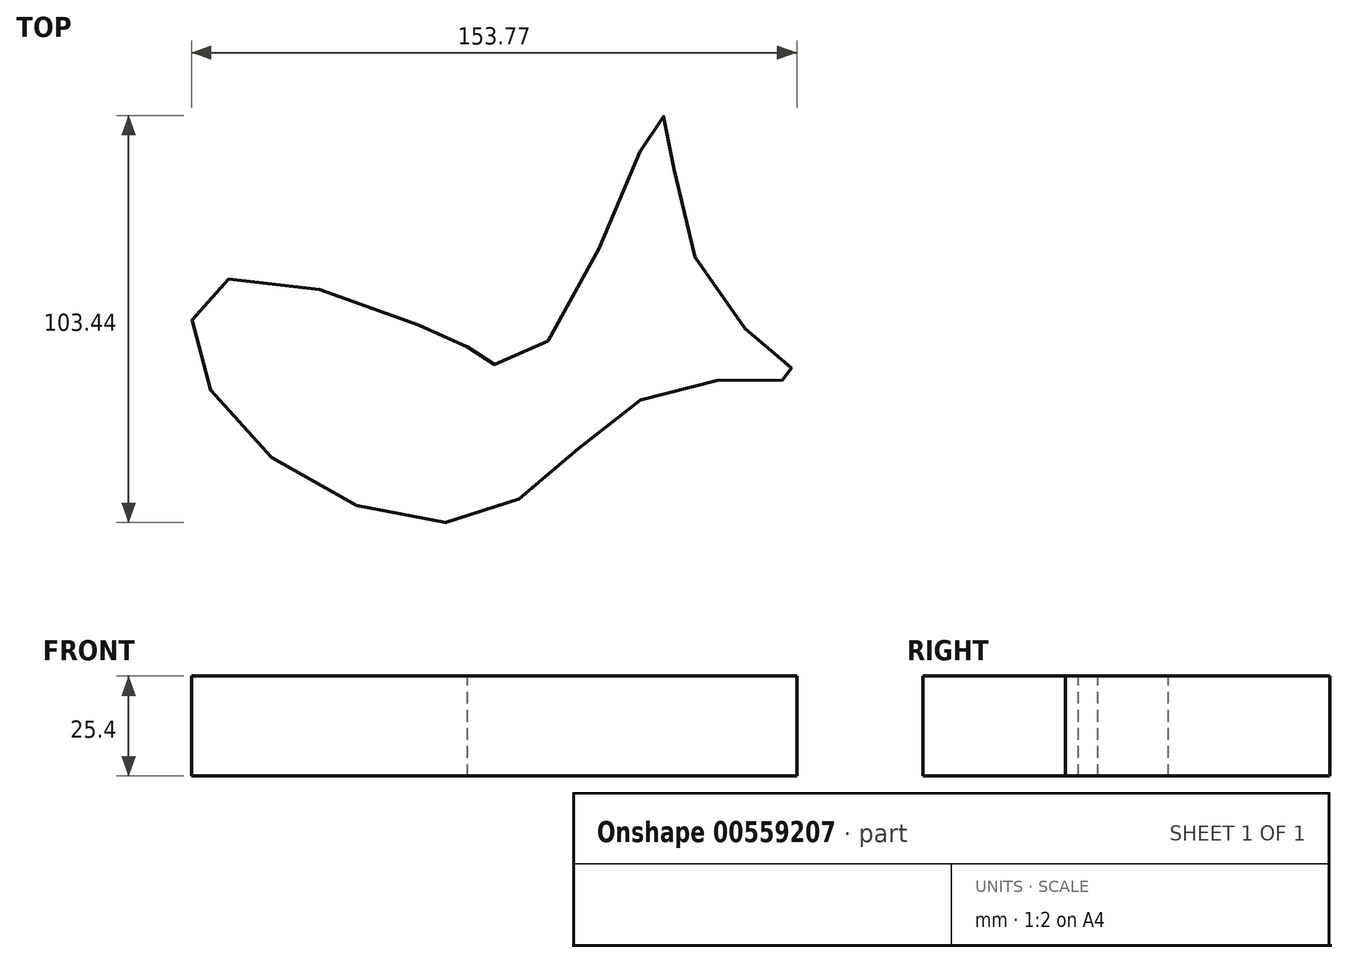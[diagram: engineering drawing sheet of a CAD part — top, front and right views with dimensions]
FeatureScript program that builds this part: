
annotation { "Feature Type Name" : "Feature", "Feature Type Description" : "" }
export const myFeature = defineFeature(function(context is Context, id is Id, definition is map)
    precondition{}
    {
        {
            var Q0;
            Q0=qCreatedBy(makeId("Top.planeOp"),FACE);
            var sketch = newSketch(context, id + "F0", { "sketchPlane" : qUnion([Q0])});
            skFitSpline(sketch, "E0", {"points": [v(-195.43, -147.8) * mm, v(-134.63, -165.12) * mm, v(-134.63, -165.12) * mm, v(-121.64, -169.64) * mm, v(-86.01, -106.47) * mm, v(-75.16, -146.08) * mm, v(-51.1, -172.61) * mm, v(-86.05, -176.4) * mm, v(-132.44, -208.65) * mm, v(-198.7, -178.08) * mm, v(-195.43, -147.8) * mm]});
            skSolve(sketch);
        }
        {
            var Q0;
            Q0=sQuery(id+"F0.wireOp",EDGE,"E0");
            extrude(context, id + "F1", {"bodyType" : ToolBodyType.SURFACE, "surfaceEntities" : qUnion([Q0]), "depth" : 25.4 * mm, "offsetDistance" : 25.4 * mm});
        }
    });
